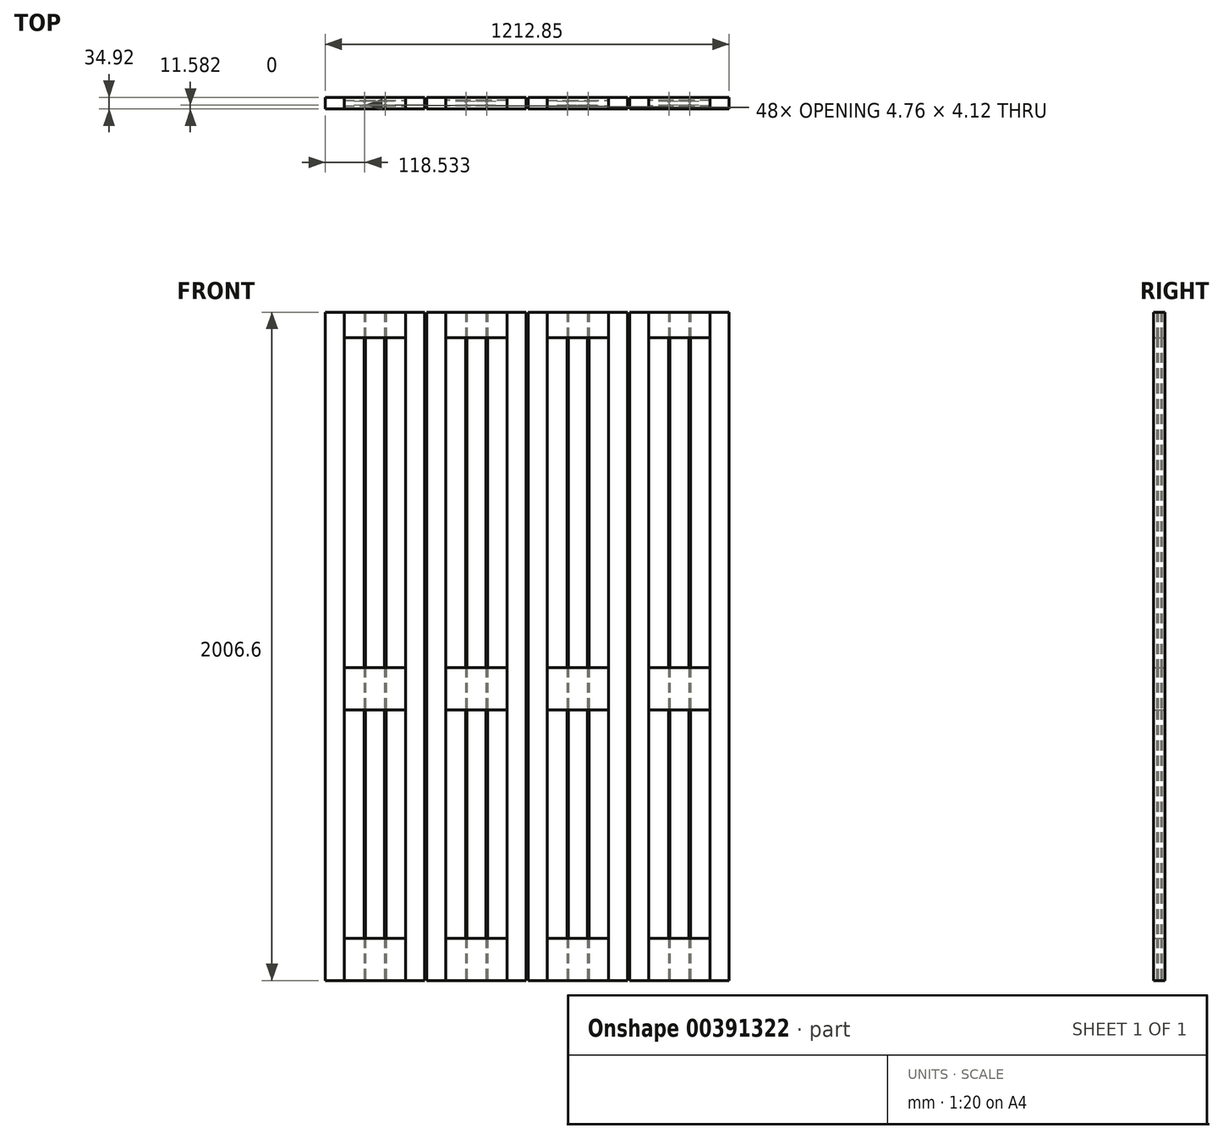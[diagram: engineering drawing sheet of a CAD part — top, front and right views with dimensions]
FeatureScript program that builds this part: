
annotation { "Feature Type Name" : "Feature", "Feature Type Description" : "" }
export const myFeature = defineFeature(function(context is Context, id is Id, definition is map)
    precondition{}
    {
        {
            var Q0;
            Q0=qCreatedBy(makeId("Front.planeOp"),FACE);
            var sketch = newSketch(context, id + "F0", { "sketchPlane" : qUnion([Q0])});
            skLineSegment(sketch, "E0.bottom", {"start": v(0, 0) * mm, "end": v(57.15, 0) * mm});
            skLineSegment(sketch, "E0.top", {"start": v(0, 2006.6) * mm, "end": v(57.15, 2006.6) * mm});
            skLineSegment(sketch, "E0.left", {"start": v(0, 0) * mm, "end": v(0, 2006.6) * mm});
            skLineSegment(sketch, "E0.right", {"start": v(57.15, 0) * mm, "end": v(57.15, 2006.6) * mm});
            skSolve(sketch);
        }
        {
            var Q0;
            Q0 = qSketchRegion(id + "F0", true);
            extrude(context, id + "F1", {"entities" : qUnion([Q0]), "depth" : 34.92 * mm});
        }
        {
            var Q0;
            Q0=qCreatedBy(makeId("Right.planeOp"),FACE);
            cPlane(context, id + "F2", {"entities" : qUnion([Q0]), "cplaneType" : CPlaneType.OFFSET, "offset" : 149.22 * mm, "width" : 152.4 * mm, "height" : 152.4 * mm});
        }
        {
            var Q0;
            Q0=makeQuery(id+"F1.opExtrude","SWEPT_BODY",BODY,{"disambiguationData":[OSD([sQuery(id+"F0.wireOp",EDGE,"E0.bottom"),sQuery(id+"F0.wireOp",EDGE,"E0.top"),sQuery(id+"F0.wireOp",EDGE,"E0.left"),sQuery(id+"F0.wireOp",EDGE,"E0.right")])]});
            var Q1;
            Q1=qCreatedBy(id+"F2.planeOp",FACE);
            mirror(context, id + "F3", {"entities" : qUnion([Q0]), "mirrorPlane" : qUnion([Q1])});
        }
        {
            var Q0;
            Q0=qCreatedBy(makeId("Front.planeOp"),FACE);
            var sketch = newSketch(context, id + "F4", { "sketchPlane" : qUnion([Q0])});
            skLineSegment(sketch, "E1.bottom", {"start": v(57.15, 2006.6) * mm, "end": v(241.3, 2006.6) * mm});
            skLineSegment(sketch, "E1.top", {"start": v(57.15, 1930.4) * mm, "end": v(241.3, 1930.4) * mm});
            skLineSegment(sketch, "E1.left", {"start": v(57.15, 2006.6) * mm, "end": v(57.15, 1930.4) * mm});
            skLineSegment(sketch, "E1.right", {"start": v(241.3, 2006.6) * mm, "end": v(241.3, 1930.4) * mm});
            skLineSegment(sketch, "E2.bottom", {"start": v(57.15, 0) * mm, "end": v(241.3, 0) * mm});
            skLineSegment(sketch, "E2.top", {"start": v(57.15, 127) * mm, "end": v(241.3, 127) * mm});
            skLineSegment(sketch, "E2.left", {"start": v(57.15, 0) * mm, "end": v(57.15, 127) * mm});
            skLineSegment(sketch, "E2.right", {"start": v(241.3, 0) * mm, "end": v(241.3, 127) * mm});
            skLineSegment(sketch, "E3.bottom", {"start": v(57.15, 939.8) * mm, "end": v(241.3, 939.8) * mm});
            skLineSegment(sketch, "E3.top", {"start": v(57.15, 812.8) * mm, "end": v(241.3, 812.8) * mm});
            skLineSegment(sketch, "E3.left", {"start": v(57.15, 939.8) * mm, "end": v(57.15, 812.8) * mm});
            skLineSegment(sketch, "E3.right", {"start": v(241.3, 939.8) * mm, "end": v(241.3, 812.8) * mm});
            skSolve(sketch);
        }
        {
            var Q0;
            Q0 = qSketchRegion(id + "F4", true);
            extrude(context, id + "F5", {"entities" : qUnion([Q0]), "depth" : 34.92 * mm});
        }
        {
            var Q0;
            Q0=qCreatedBy(makeId("Front.planeOp"),FACE);
            cPlane(context, id + "F6", {"entities" : qUnion([Q0]), "cplaneType" : CPlaneType.OFFSET, "offset" : 9.52 * mm, "width" : 152.4 * mm, "height" : 152.4 * mm});
        }
        {
            var Q0;
            Q0=qCreatedBy(id+"F6.planeOp",FACE);
            var sketch = newSketch(context, id + "F7", { "sketchPlane" : qUnion([Q0])});
            skLineSegment(sketch, "E4.bottom", {"start": v(57.15, 1930.4) * mm, "end": v(103.19, 1930.4) * mm});
            skLineSegment(sketch, "E4.top", {"start": v(57.15, 939.8) * mm, "end": v(103.19, 939.8) * mm});
            skLineSegment(sketch, "E4.left", {"start": v(57.15, 1930.4) * mm, "end": v(57.15, 939.8) * mm});
            skLineSegment(sketch, "E4.right", {"start": v(103.19, 1930.4) * mm, "end": v(103.19, 939.8) * mm});
            skLineSegment(sketch, "E5.bottom", {"start": v(103.19, 1930.4) * mm, "end": v(149.22, 1930.4) * mm});
            skLineSegment(sketch, "E5.top", {"start": v(103.19, 939.8) * mm, "end": v(149.23, 939.8) * mm});
            skLineSegment(sketch, "E5.right", {"start": v(149.22, 1930.4) * mm, "end": v(149.23, 939.8) * mm});
            skLineSegment(sketch, "E6.bottom", {"start": v(149.22, 1930.4) * mm, "end": v(195.26, 1930.4) * mm});
            skLineSegment(sketch, "E6.top", {"start": v(149.23, 939.8) * mm, "end": v(195.26, 939.8) * mm});
            skLineSegment(sketch, "E6.right", {"start": v(195.26, 1930.4) * mm, "end": v(195.26, 939.8) * mm});
            skLineSegment(sketch, "E7.bottom", {"start": v(195.26, 1930.4) * mm, "end": v(241.3, 1930.4) * mm});
            skLineSegment(sketch, "E7.top", {"start": v(195.26, 939.8) * mm, "end": v(241.3, 939.8) * mm});
            skLineSegment(sketch, "E7.right", {"start": v(241.3, 1930.4) * mm, "end": v(241.3, 939.8) * mm});
            skLineSegment(sketch, "E8.bottom", {"start": v(57.46, 812.8) * mm, "end": v(103.5, 812.8) * mm});
            skLineSegment(sketch, "E8.top", {"start": v(57.46, 127) * mm, "end": v(103.5, 127) * mm});
            skLineSegment(sketch, "E8.left", {"start": v(57.46, 812.8) * mm, "end": v(57.46, 127) * mm});
            skLineSegment(sketch, "E8.right", {"start": v(103.5, 812.8) * mm, "end": v(103.5, 127) * mm});
            skLineSegment(sketch, "E9.bottom", {"start": v(103.5, 812.8) * mm, "end": v(149.53, 812.8) * mm});
            skLineSegment(sketch, "E9.top", {"start": v(103.5, 127) * mm, "end": v(149.53, 127) * mm});
            skLineSegment(sketch, "E9.right", {"start": v(149.53, 812.8) * mm, "end": v(149.53, 127) * mm});
            skLineSegment(sketch, "E10.bottom", {"start": v(149.53, 812.8) * mm, "end": v(195.57, 812.8) * mm});
            skLineSegment(sketch, "E10.top", {"start": v(149.53, 127) * mm, "end": v(195.57, 127) * mm});
            skLineSegment(sketch, "E10.right", {"start": v(195.57, 812.8) * mm, "end": v(195.57, 127) * mm});
            skLineSegment(sketch, "E11.bottom", {"start": v(195.57, 812.8) * mm, "end": v(241.6, 812.8) * mm});
            skLineSegment(sketch, "E11.top", {"start": v(195.57, 127) * mm, "end": v(241.6, 127) * mm});
            skLineSegment(sketch, "E11.right", {"start": v(241.6, 812.8) * mm, "end": v(241.6, 127) * mm});
            skSolve(sketch);
        }
        {
            var Q0;
            Q0 = qSketchRegion(id + "F7", true);
            extrude(context, id + "F8", {"entities" : qUnion([Q0]), "depth" : 15.88 * mm});
        }
        {
            var Q0;
            Q0=qCreatedBy(id+"F6.planeOp",FACE);
            cPlane(context, id + "F9", {"entities" : qUnion([Q0]), "cplaneType" : CPlaneType.OFFSET, "offset" : 7.94 * mm, "width" : 152.4 * mm, "height" : 152.4 * mm});
        }
        {
            var Q0;
            Q0=qCreatedBy(makeId("Top.planeOp"),FACE);
            var sketch = newSketch(context, id + "F10", { "sketchPlane" : qUnion([Q0])});
            skLineSegment(sketch, "E12", {"start": v(116.15, -9.52) * mm, "end": v(118.53, -13.65) * mm});
            skLineSegment(sketch, "E13", {"start": v(118.53, -13.65) * mm, "end": v(120.91, -9.52) * mm});
            skLineSegment(sketch, "E14", {"start": v(120.91, -9.53) * mm, "end": v(116.15, -9.53) * mm});
            skLineSegment(sketch, "E15", {"start": v(177.54, -9.52) * mm, "end": v(179.92, -13.65) * mm});
            skLineSegment(sketch, "E16", {"start": v(179.92, -13.65) * mm, "end": v(182.3, -9.52) * mm});
            skLineSegment(sketch, "E17", {"start": v(182.3, -9.52) * mm, "end": v(177.54, -9.52) * mm});
            skPoint(sketch, "E18.orphan", {"position": v(118.53, -13.65) * mm});
            skPoint(sketch, "E19.orphan", {"position": v(179.92, -13.65) * mm});
            skPoint(sketch, "E20.orphan", {"position": v(103.19, -9.53) * mm});
            skLineSegment(sketch, "E21.MirrorCS", {"start": v(118.53, -21.28) * mm, "end": v(120.91, -25.4) * mm});
            skLineSegment(sketch, "E22.MirrorCS", {"start": v(120.91, -25.4) * mm, "end": v(116.15, -25.4) * mm});
            skPoint(sketch, "E23.MirrorP", {"position": v(103.19, -25.4) * mm});
            skPoint(sketch, "E24.MirrorP", {"position": v(179.92, -21.28) * mm});
            skLineSegment(sketch, "E25.MirrorCS", {"start": v(179.92, -21.28) * mm, "end": v(182.3, -25.4) * mm});
            skLineSegment(sketch, "E26.MirrorCS", {"start": v(177.54, -25.4) * mm, "end": v(179.92, -21.28) * mm});
            skLineSegment(sketch, "E27.MirrorCS", {"start": v(116.15, -25.4) * mm, "end": v(118.53, -21.28) * mm});
            skPoint(sketch, "E28.MirrorP", {"position": v(118.53, -21.28) * mm});
            skLineSegment(sketch, "E29.MirrorCS", {"start": v(182.3, -25.4) * mm, "end": v(177.54, -25.4) * mm});
            skSolve(sketch);
        }
        {
            var Q0;
            Q0 = qSketchRegion(id + "F10", true);
            extrude(context, id + "F11", {"entities" : qUnion([Q0]), "operationType" : NewBodyOperationType.REMOVE, "endBound" : BoundingType.THROUGH_ALL, "depth" : 25.4 * mm});
        }
        {
            var Q0;
            Q0=qCreatedBy(makeId("Right.planeOp"),FACE);
            cPlane(context, id + "F12", {"entities" : qUnion([Q0]), "cplaneType" : CPlaneType.OFFSET, "offset" : 301.62 * mm, "width" : 152.4 * mm, "height" : 152.4 * mm});
        }
        {
            var Q0;
            Q0=qCreatedBy(makeId("Right.planeOp"),FACE);
            cPlane(context, id + "F13", {"entities" : qUnion([Q0]), "cplaneType" : CPlaneType.OFFSET, "offset" : 606.42 * mm, "width" : 152.4 * mm, "height" : 152.4 * mm});
        }
        {
            var Q0;
            Q0=makeQuery(id+"F5.opExtrude","SWEPT_BODY",BODY,{"disambiguationData":[OSD([sQuery(id+"F4.wireOp",EDGE,"E3.bottom"),sQuery(id+"F4.wireOp",EDGE,"E3.top"),sQuery(id+"F4.wireOp",EDGE,"E3.left"),sQuery(id+"F4.wireOp",EDGE,"E3.right")])]});
            var Q1;
            Q1=makeQuery(id+"F5.opExtrude","SWEPT_BODY",BODY,{"disambiguationData":[OSD([sQuery(id+"F4.wireOp",EDGE,"E1.bottom"),sQuery(id+"F4.wireOp",EDGE,"E1.top"),sQuery(id+"F4.wireOp",EDGE,"E1.left"),sQuery(id+"F4.wireOp",EDGE,"E1.right")])]});
            var Q2;
            Q2=makeQuery(id+"F5.opExtrude","SWEPT_BODY",BODY,{"disambiguationData":[OSD([sQuery(id+"F4.wireOp",EDGE,"E2.bottom"),sQuery(id+"F4.wireOp",EDGE,"E2.top"),sQuery(id+"F4.wireOp",EDGE,"E2.left"),sQuery(id+"F4.wireOp",EDGE,"E2.right")])]});
            var Q3;
            Q3=makeQuery(id+"F3.opPattern","COPY",BODY,{"derivedFrom":makeQuery(id+"F1.opExtrude","SWEPT_BODY",BODY,{"disambiguationData":[OSD([sQuery(id+"F0.wireOp",EDGE,"E0.bottom"),sQuery(id+"F0.wireOp",EDGE,"E0.top"),sQuery(id+"F0.wireOp",EDGE,"E0.left"),sQuery(id+"F0.wireOp",EDGE,"E0.right")])]}),"instanceName":"1"});
            var Q4;
            Q4=makeQuery(id+"F1.opExtrude","SWEPT_BODY",BODY,{"disambiguationData":[OSD([sQuery(id+"F0.wireOp",EDGE,"E0.bottom"),sQuery(id+"F0.wireOp",EDGE,"E0.top"),sQuery(id+"F0.wireOp",EDGE,"E0.left"),sQuery(id+"F0.wireOp",EDGE,"E0.right")])]});
            var Q5;
            Q5=makeQuery(id+"F8.opExtrude","SWEPT_BODY",BODY,{"disambiguationData":[OSD([sQuery(id+"F7.wireOp",EDGE,"E8.bottom"),sQuery(id+"F7.wireOp",EDGE,"E8.top"),sQuery(id+"F7.wireOp",EDGE,"E8.left"),sQuery(id+"F7.wireOp",EDGE,"E9.bottom"),sQuery(id+"F7.wireOp",EDGE,"E9.top"),sQuery(id+"F7.wireOp",EDGE,"E10.bottom"),sQuery(id+"F7.wireOp",EDGE,"E10.top"),sQuery(id+"F7.wireOp",EDGE,"E11.bottom"),sQuery(id+"F7.wireOp",EDGE,"E11.top"),sQuery(id+"F7.wireOp",EDGE,"E11.right")])]});
            var Q6;
            Q6=makeQuery(id+"F8.opExtrude","SWEPT_BODY",BODY,{"disambiguationData":[OSD([sQuery(id+"F7.wireOp",EDGE,"E4.bottom"),sQuery(id+"F7.wireOp",EDGE,"E4.top"),sQuery(id+"F7.wireOp",EDGE,"E4.left"),sQuery(id+"F7.wireOp",EDGE,"E5.bottom"),sQuery(id+"F7.wireOp",EDGE,"E5.top"),sQuery(id+"F7.wireOp",EDGE,"E6.bottom"),sQuery(id+"F7.wireOp",EDGE,"E6.top"),sQuery(id+"F7.wireOp",EDGE,"E7.bottom"),sQuery(id+"F7.wireOp",EDGE,"E7.top"),sQuery(id+"F7.wireOp",EDGE,"E7.right")])]});
            var Q7;
            Q7=qCreatedBy(id+"F12.planeOp",FACE);
            mirror(context, id + "F14", {"entities" : qUnion([Q0, Q1, Q2, Q3, Q4, Q5, Q6]), "mirrorPlane" : qUnion([Q7])});
        }
        {
            var Q0;
            Q0=makeQuery(id+"F5.opExtrude","SWEPT_BODY",BODY,{"disambiguationData":[OSD([sQuery(id+"F4.wireOp",EDGE,"E3.bottom"),sQuery(id+"F4.wireOp",EDGE,"E3.top"),sQuery(id+"F4.wireOp",EDGE,"E3.left"),sQuery(id+"F4.wireOp",EDGE,"E3.right")])]});
            var Q1;
            Q1=makeQuery(id+"F5.opExtrude","SWEPT_BODY",BODY,{"disambiguationData":[OSD([sQuery(id+"F4.wireOp",EDGE,"E1.bottom"),sQuery(id+"F4.wireOp",EDGE,"E1.top"),sQuery(id+"F4.wireOp",EDGE,"E1.left"),sQuery(id+"F4.wireOp",EDGE,"E1.right")])]});
            var Q2;
            Q2=makeQuery(id+"F5.opExtrude","SWEPT_BODY",BODY,{"disambiguationData":[OSD([sQuery(id+"F4.wireOp",EDGE,"E2.bottom"),sQuery(id+"F4.wireOp",EDGE,"E2.top"),sQuery(id+"F4.wireOp",EDGE,"E2.left"),sQuery(id+"F4.wireOp",EDGE,"E2.right")])]});
            var Q3;
            Q3=makeQuery(id+"F3.opPattern","COPY",BODY,{"derivedFrom":makeQuery(id+"F1.opExtrude","SWEPT_BODY",BODY,{"disambiguationData":[OSD([sQuery(id+"F0.wireOp",EDGE,"E0.bottom"),sQuery(id+"F0.wireOp",EDGE,"E0.top"),sQuery(id+"F0.wireOp",EDGE,"E0.left"),sQuery(id+"F0.wireOp",EDGE,"E0.right")])]}),"instanceName":"1"});
            var Q4;
            Q4=makeQuery(id+"F1.opExtrude","SWEPT_BODY",BODY,{"disambiguationData":[OSD([sQuery(id+"F0.wireOp",EDGE,"E0.bottom"),sQuery(id+"F0.wireOp",EDGE,"E0.top"),sQuery(id+"F0.wireOp",EDGE,"E0.left"),sQuery(id+"F0.wireOp",EDGE,"E0.right")])]});
            var Q5;
            Q5=makeQuery(id+"F14.opPattern","COPY",BODY,{"derivedFrom":makeQuery(id+"F8.opExtrude","SWEPT_BODY",BODY,{"disambiguationData":[OSD([sQuery(id+"F7.wireOp",EDGE,"E4.bottom"),sQuery(id+"F7.wireOp",EDGE,"E4.top"),sQuery(id+"F7.wireOp",EDGE,"E4.left"),sQuery(id+"F7.wireOp",EDGE,"E5.bottom"),sQuery(id+"F7.wireOp",EDGE,"E5.top"),sQuery(id+"F7.wireOp",EDGE,"E6.bottom"),sQuery(id+"F7.wireOp",EDGE,"E6.top"),sQuery(id+"F7.wireOp",EDGE,"E7.bottom"),sQuery(id+"F7.wireOp",EDGE,"E7.top"),sQuery(id+"F7.wireOp",EDGE,"E7.right")])]}),"instanceName":"1"});
            var Q6;
            Q6=makeQuery(id+"F14.opPattern","COPY",BODY,{"derivedFrom":makeQuery(id+"F1.opExtrude","SWEPT_BODY",BODY,{"disambiguationData":[OSD([sQuery(id+"F0.wireOp",EDGE,"E0.bottom"),sQuery(id+"F0.wireOp",EDGE,"E0.top"),sQuery(id+"F0.wireOp",EDGE,"E0.left"),sQuery(id+"F0.wireOp",EDGE,"E0.right")])]}),"instanceName":"1"});
            var Q7;
            Q7=makeQuery(id+"F14.opPattern","COPY",BODY,{"derivedFrom":makeQuery(id+"F5.opExtrude","SWEPT_BODY",BODY,{"disambiguationData":[OSD([sQuery(id+"F4.wireOp",EDGE,"E3.bottom"),sQuery(id+"F4.wireOp",EDGE,"E3.top"),sQuery(id+"F4.wireOp",EDGE,"E3.left"),sQuery(id+"F4.wireOp",EDGE,"E3.right")])]}),"instanceName":"1"});
            var Q8;
            Q8=makeQuery(id+"F14.opPattern","COPY",BODY,{"derivedFrom":makeQuery(id+"F8.opExtrude","SWEPT_BODY",BODY,{"disambiguationData":[OSD([sQuery(id+"F7.wireOp",EDGE,"E8.bottom"),sQuery(id+"F7.wireOp",EDGE,"E8.top"),sQuery(id+"F7.wireOp",EDGE,"E8.left"),sQuery(id+"F7.wireOp",EDGE,"E9.bottom"),sQuery(id+"F7.wireOp",EDGE,"E9.top"),sQuery(id+"F7.wireOp",EDGE,"E10.bottom"),sQuery(id+"F7.wireOp",EDGE,"E10.top"),sQuery(id+"F7.wireOp",EDGE,"E11.bottom"),sQuery(id+"F7.wireOp",EDGE,"E11.top"),sQuery(id+"F7.wireOp",EDGE,"E11.right")])]}),"instanceName":"1"});
            var Q9;
            Q9=makeQuery(id+"F14.opPattern","COPY",BODY,{"derivedFrom":makeQuery(id+"F5.opExtrude","SWEPT_BODY",BODY,{"disambiguationData":[OSD([sQuery(id+"F4.wireOp",EDGE,"E2.bottom"),sQuery(id+"F4.wireOp",EDGE,"E2.top"),sQuery(id+"F4.wireOp",EDGE,"E2.left"),sQuery(id+"F4.wireOp",EDGE,"E2.right")])]}),"instanceName":"1"});
            var Q10;
            Q10=makeQuery(id+"F14.opPattern","COPY",BODY,{"derivedFrom":makeQuery(id+"F5.opExtrude","SWEPT_BODY",BODY,{"disambiguationData":[OSD([sQuery(id+"F4.wireOp",EDGE,"E1.bottom"),sQuery(id+"F4.wireOp",EDGE,"E1.top"),sQuery(id+"F4.wireOp",EDGE,"E1.left"),sQuery(id+"F4.wireOp",EDGE,"E1.right")])]}),"instanceName":"1"});
            var Q11;
            Q11=makeQuery(id+"F14.opPattern","COPY",BODY,{"derivedFrom":makeQuery(id+"F3.opPattern","COPY",BODY,{"derivedFrom":makeQuery(id+"F1.opExtrude","SWEPT_BODY",BODY,{"disambiguationData":[OSD([sQuery(id+"F0.wireOp",EDGE,"E0.bottom"),sQuery(id+"F0.wireOp",EDGE,"E0.top"),sQuery(id+"F0.wireOp",EDGE,"E0.left"),sQuery(id+"F0.wireOp",EDGE,"E0.right")])]}),"instanceName":"1"}),"instanceName":"1"});
            var Q12;
            Q12=makeQuery(id+"F8.opExtrude","SWEPT_BODY",BODY,{"disambiguationData":[OSD([sQuery(id+"F7.wireOp",EDGE,"E8.bottom"),sQuery(id+"F7.wireOp",EDGE,"E8.top"),sQuery(id+"F7.wireOp",EDGE,"E8.left"),sQuery(id+"F7.wireOp",EDGE,"E9.bottom"),sQuery(id+"F7.wireOp",EDGE,"E9.top"),sQuery(id+"F7.wireOp",EDGE,"E10.bottom"),sQuery(id+"F7.wireOp",EDGE,"E10.top"),sQuery(id+"F7.wireOp",EDGE,"E11.bottom"),sQuery(id+"F7.wireOp",EDGE,"E11.top"),sQuery(id+"F7.wireOp",EDGE,"E11.right")])]});
            var Q13;
            Q13=makeQuery(id+"F8.opExtrude","SWEPT_BODY",BODY,{"disambiguationData":[OSD([sQuery(id+"F7.wireOp",EDGE,"E4.bottom"),sQuery(id+"F7.wireOp",EDGE,"E4.top"),sQuery(id+"F7.wireOp",EDGE,"E4.left"),sQuery(id+"F7.wireOp",EDGE,"E5.bottom"),sQuery(id+"F7.wireOp",EDGE,"E5.top"),sQuery(id+"F7.wireOp",EDGE,"E6.bottom"),sQuery(id+"F7.wireOp",EDGE,"E6.top"),sQuery(id+"F7.wireOp",EDGE,"E7.bottom"),sQuery(id+"F7.wireOp",EDGE,"E7.top"),sQuery(id+"F7.wireOp",EDGE,"E7.right")])]});
            var Q14;
            Q14=qCreatedBy(id+"F13.planeOp",FACE);
            mirror(context, id + "F15", {"entities" : qUnion([Q0, Q1, Q2, Q3, Q4, Q5, Q6, Q7, Q8, Q9, Q10, Q11, Q12, Q13]), "mirrorPlane" : qUnion([Q14])});
        }
    });
